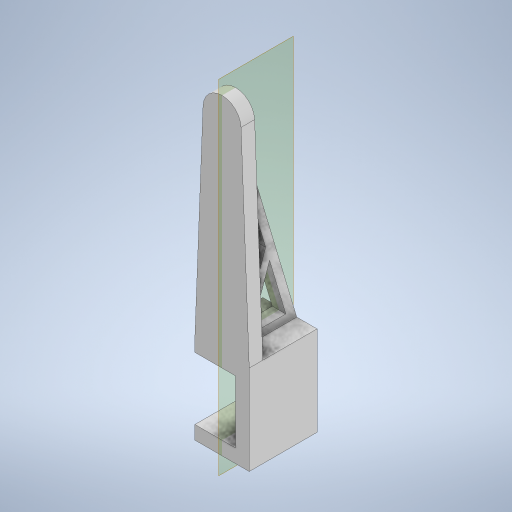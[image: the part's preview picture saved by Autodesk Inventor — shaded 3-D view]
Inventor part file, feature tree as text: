
AUTODESK INVENTOR PART (.ipt)
format: ipt  version: 2023 (Build 270158000, 158)  size: 284,672 bytes
history: native  units: mm
features: extrude x3, sketch x3, other x2
ambient origin geometry x8: Origin, YZ Plane, XZ Plane, XY Plane, X Axis, Y Axis, Z Axis, Center Point
bodies: Body1 (feature_tree)
feature tree (8):
  other  "솔리드1"
  extrude  "돌출1"  Depth=66.0mm
  extrude  "돌출2"  Depth=10.0mm
  other  "작업 평면1"
  extrude  "돌출3"  Depth=10.0mm
  sketch  "스케치1"
  sketch  "스케치2"
  sketch  "스케치3"
